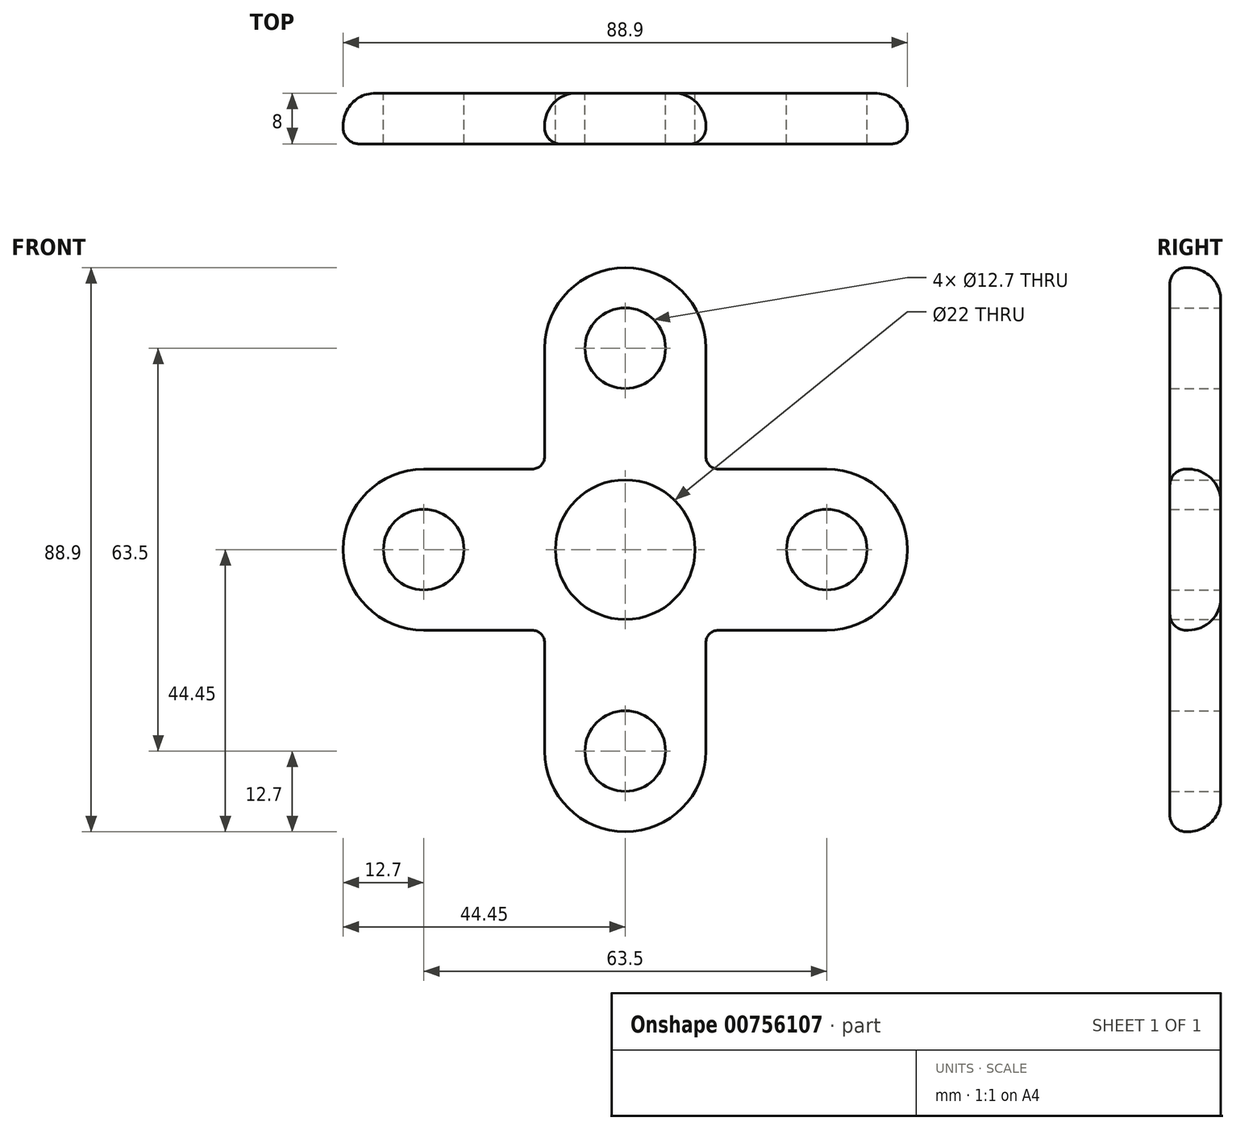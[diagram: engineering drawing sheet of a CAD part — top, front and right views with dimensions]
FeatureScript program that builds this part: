
annotation { "Feature Type Name" : "Feature", "Feature Type Description" : "" }
export const myFeature = defineFeature(function(context is Context, id is Id, definition is map)
    precondition{}
    {
        {
            var Q0;
            Q0=qCreatedBy(makeId("Front.planeOp"),FACE);
            var sketch = newSketch(context, id + "F0", { "sketchPlane" : qUnion([Q0])});
            skLineSegment(sketch, "E0.bottom", {"start": v(-31.75, -12.7) * mm, "end": v(31.75, -12.7) * mm});
            skLineSegment(sketch, "E0.top", {"start": v(-31.75, 12.7) * mm, "end": v(31.75, 12.7) * mm});
            skLineSegment(sketch, "E0.left", {"start": v(-31.75, -12.7) * mm, "end": v(-31.75, 12.7) * mm});
            skLineSegment(sketch, "E0.right", {"start": v(31.75, -12.7) * mm, "end": v(31.75, 12.7) * mm});
            skPoint(sketch, "E0.middle", {"position": v(0, 0) * mm});
            skLineSegment(sketch, "E1.bottom", {"start": v(-12.7, 31.75) * mm, "end": v(12.7, 31.75) * mm});
            skLineSegment(sketch, "E1.top", {"start": v(-12.7, -31.75) * mm, "end": v(12.7, -31.75) * mm});
            skLineSegment(sketch, "E1.left", {"start": v(-12.7, 31.75) * mm, "end": v(-12.7, -31.75) * mm});
            skLineSegment(sketch, "E1.right", {"start": v(12.7, 31.75) * mm, "end": v(12.7, -31.75) * mm});
            skLineSegment(sketch, "E2", {"start": v(-31.75, 0) * mm, "end": v(31.75, 0) * mm});
            skLineSegment(sketch, "E3", {"start": v(0, -31.75) * mm, "end": v(0, 31.75) * mm});
            skCircle(sketch, "E4", {"center": v(-31.75, 0) * mm, "radius": 12.7 * mm});
            skCircle(sketch, "E5", {"center": v(0, 31.75) * mm, "radius": 12.7 * mm});
            skCircle(sketch, "E6", {"center": v(31.75, 0) * mm, "radius": 12.7 * mm});
            skCircle(sketch, "E7", {"center": v(0, -31.75) * mm, "radius": 12.7 * mm});
            skCircle(sketch, "E8", {"center": v(-31.75, 0) * mm, "radius": 6.35 * mm});
            skCircle(sketch, "E9", {"center": v(0, -31.75) * mm, "radius": 6.35 * mm});
            skCircle(sketch, "E10", {"center": v(31.75, 0) * mm, "radius": 6.35 * mm});
            skCircle(sketch, "E11", {"center": v(0, 31.75) * mm, "radius": 6.35 * mm});
            skCircle(sketch, "E12", {"center": v(0, 0) * mm, "radius": 11 * mm});
            skSolve(sketch);
        }
        {
            var Q0;
            Q0 = qSketchRegion(id + "F0", true);
            extrude(context, id + "F1", {"entities" : qUnion([Q0]), "endBound" : BoundingType.SYMMETRIC, "depth" : 8 * mm, "offsetDistance" : 25.4 * mm});
        }
        {
            var Q0;
            Q0=makeQuery(id+"F1.opExtrude","SWEPT_EDGE",EDGE,{"disambiguationData":[OSD([sQuery(id+"F0.wireOp",EDGE,"E0.top"),sQuery(id+"F0.wireOp",EDGE,"E1.right")])]});
            var Q1;
            Q1=makeQuery(id+"F1.opExtrude","SWEPT_EDGE",EDGE,{"disambiguationData":[OSD([sQuery(id+"F0.wireOp",EDGE,"E0.bottom"),sQuery(id+"F0.wireOp",EDGE,"E1.right")])]});
            var Q2;
            Q2=makeQuery(id+"F1.opExtrude","SWEPT_EDGE",EDGE,{"disambiguationData":[OSD([sQuery(id+"F0.wireOp",EDGE,"E0.bottom"),sQuery(id+"F0.wireOp",EDGE,"E1.left")])]});
            var Q3;
            Q3=makeQuery(id+"F1.opExtrude","SWEPT_EDGE",EDGE,{"disambiguationData":[OSD([sQuery(id+"F0.wireOp",EDGE,"E0.top"),sQuery(id+"F0.wireOp",EDGE,"E1.left")])]});
            fillet(context, id + "F2", {"entities" : qUnion([Q0, Q1, Q2, Q3]), "radius" : 2 * mm, "tangentPropagation" : true, "allowEdgeOverflow" : false});
        }
        {
            var Q0;
            {var subQ0=sQuery(id+"F0.wireOp",EDGE,"E0.top");Q0=makeQuery(id+"F1.opExtrude","CAP_EDGE",EDGE,{"disambiguationData":[OSD([subQ0]),TDD([makeQuery(id+"F0.imprint","IMPRINT",EDGE,{"disambiguationData":[TD([[makeQuery(id+"F0.imprint","INTERSECT",VERTEX,{"derivedFrom":[subQ0,sQuery(id+"F0.wireOp",EDGE,"E1.right")]}),-1.0]])],"derivedFrom":subQ0})])],"isStart":true});}
            fillet(context, id + "F3", {"entities" : qUnion([Q0]), "radius" : 5.08 * mm, "tangentPropagation" : true, "allowEdgeOverflow" : false});
        }
        {
            var Q0;
            {var subQ0=sQuery(id+"F0.wireOp",EDGE,"E1.right");Q0=makeQuery(id+"F1.opExtrude","CAP_EDGE",EDGE,{"disambiguationData":[OSD([subQ0]),TDD([makeQuery(id+"F0.imprint","IMPRINT",EDGE,{"disambiguationData":[TD([[makeQuery(id+"F0.imprint","INTERSECT",VERTEX,{"derivedFrom":[sQuery(id+"F0.wireOp",EDGE,"E0.top"),subQ0]}),1.0]])],"derivedFrom":subQ0})])],"isStart":false});}
            fillet(context, id + "F4", {"entities" : qUnion([Q0]), "radius" : 2.54 * mm, "tangentPropagation" : true, "allowEdgeOverflow" : false});
        }
    });
